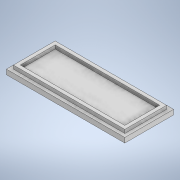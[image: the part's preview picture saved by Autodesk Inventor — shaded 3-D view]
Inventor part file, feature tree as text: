
AUTODESK INVENTOR PART (.ipt)
format: ipt  version: 2020 (Build 240168000, 168)  size: 120,320 bytes
history: native  units: mm
features: extrude x2, sketch x2
ambient origin geometry x8: Origin, YZ Plane, XZ Plane, XY Plane, X Axis, Y Axis, Z Axis, Center Point
bodies: Solid1 (feature_tree)
feature tree (4):
  extrude  "Extrusion1"  Depth=70.0mm
  extrude  "Extrusion2"  Depth=5.0mm
  sketch  "Sketch1"  dims[d0=170.0mm d1=70.0mm]
  sketch  "Sketch2"  dims[d2=7.0mm d3=0.0mm d4=5.0mm d5=5.0mm d6=5.0mm d7=5.0mm d8=5.0mm d9=5.0mm d10=5.0mm d11=5.0mm d12=5.0mm d13=0.0mm]
